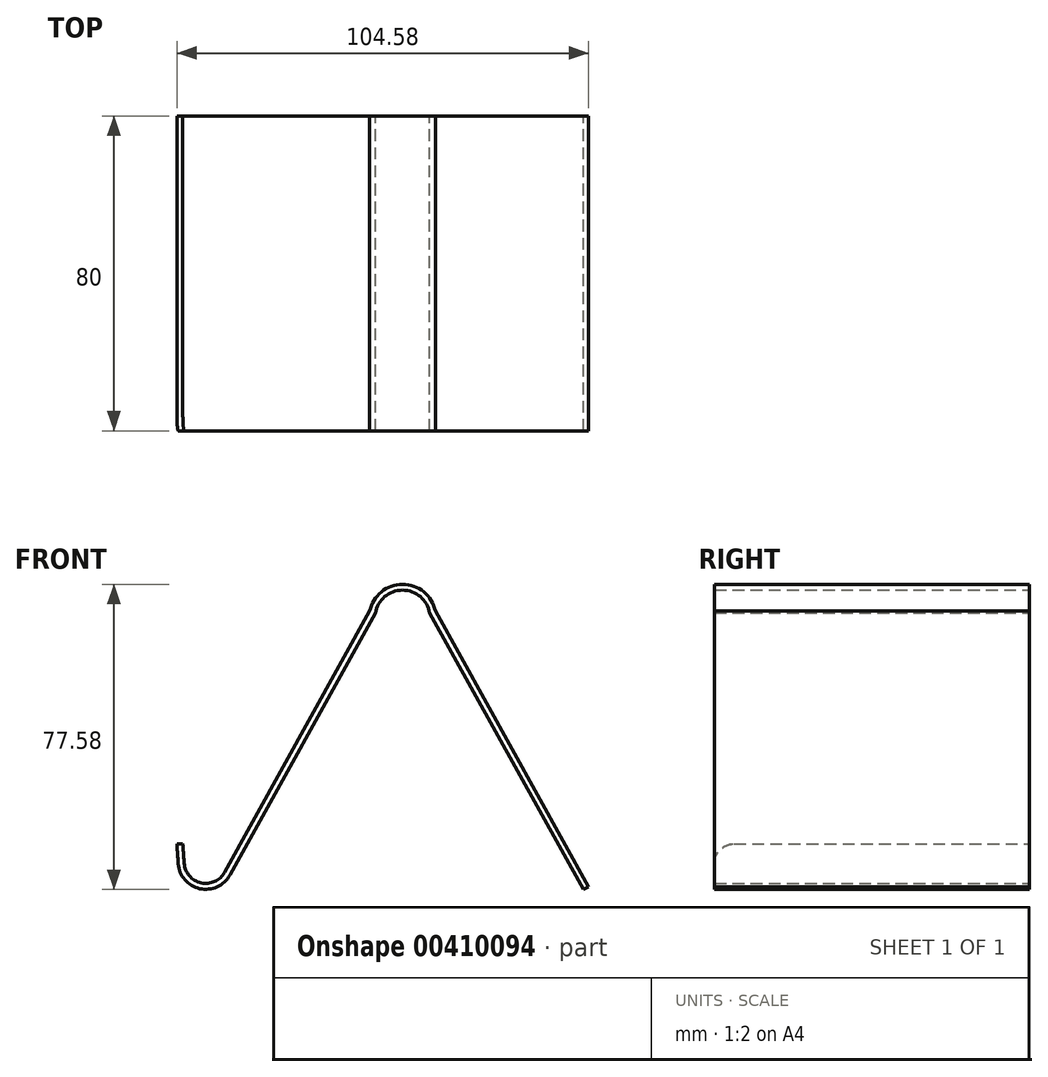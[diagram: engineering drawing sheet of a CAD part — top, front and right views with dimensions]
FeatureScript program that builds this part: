
annotation { "Feature Type Name" : "Feature", "Feature Type Description" : "" }
export const myFeature = defineFeature(function(context is Context, id is Id, definition is map)
    precondition{}
    {
        {
            var Q0;
            Q0=qCreatedBy(makeId("Front.planeOp"),FACE);
            var sketch = newSketch(context, id + "F0", { "sketchPlane" : qUnion([Q0])});
            skArc(sketch, "E0", {"start": v(-66.84, 6.62) * mm, "mid": v(-61.37, 0.29) * mm, "end": v(-53.74, 3.72) * mm});
            skArc(sketch, "E1", {"start": v(-2.95, 70.27) * mm, "mid": v(-9.86, 76.12) * mm, "end": v(-16.76, 70.27) * mm});
            skLineSegment(sketch, "E2", {"start": v(-53.74, 3.72) * mm, "end": v(-16.76, 70.27) * mm});
            skLineSegment(sketch, "E3", {"start": v(-9.86, 69.12) * mm, "end": v(-9.86, 0) * mm, "construction": true});
            skLineSegment(sketch, "E4.MirrorCS", {"start": v(36.07, 0.04) * mm, "end": v(-2.95, 70.27) * mm});
            skLineSegment(sketch, "E5", {"start": v(-60.21, 0.13) * mm, "end": v(78.05, 0) * mm, "construction": true});
            skPoint(sketch, "E6.orphan", {"position": v(34.02, 3.72) * mm});
            skLineSegment(sketch, "E7", {"start": v(-66.84, 6.62) * mm, "end": v(-67.2, 11.6) * mm});
            skLineSegment(sketch, "E8.0", {"start": v(-65.34, 6.73) * mm, "end": v(-65.7, 11.72) * mm});
            skLineSegment(sketch, "E8.1", {"start": v(37.38, 0.77) * mm, "end": v(-1.52, 70.79) * mm});
            skArc(sketch, "E8.2", {"start": v(-1.52, 70.79) * mm, "mid": v(-9.86, 77.62) * mm, "end": v(-18.2, 70.79) * mm});
            skLineSegment(sketch, "E8.3", {"start": v(-55.05, 4.45) * mm, "end": v(-18.2, 70.79) * mm});
            skArc(sketch, "E8.4", {"start": v(-65.34, 6.73) * mm, "mid": v(-61.05, 1.75) * mm, "end": v(-55.05, 4.45) * mm});
            skLineSegment(sketch, "E9", {"start": v(36.07, 0.04) * mm, "end": v(37.38, 0.77) * mm});
            skLineSegment(sketch, "E10", {"start": v(-67.2, 11.6) * mm, "end": v(-65.7, 11.72) * mm});
            skSolve(sketch);
        }
        {
            var Q0;
            Q0=makeQuery(id+"F0.imprint","IMPRINT",FACE,{"disambiguationData":[TD([[makeQuery(id+"F0.imprint","IMPRINT",EDGE,{"derivedFrom":sQuery(id+"F0.wireOp",EDGE,"E0")}),1.0]])]});
            extrude(context, id + "F1", {"entities" : qUnion([Q0]), "depth" : 80 * mm});
        }
        {
            var Q0;
            Q0=makeQuery(id+"F1.opExtrude","CAP_EDGE",EDGE,{"disambiguationData":[OSD([sQuery(id+"F0.wireOp",EDGE,"E10")])],"isStart":false});
            fillet(context, id + "F2", {"entities" : qUnion([Q0]), "radius" : 5 * mm, "tangentPropagation" : true, "allowEdgeOverflow" : false});
        }
    });
